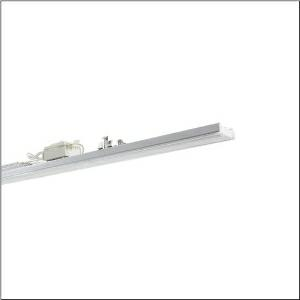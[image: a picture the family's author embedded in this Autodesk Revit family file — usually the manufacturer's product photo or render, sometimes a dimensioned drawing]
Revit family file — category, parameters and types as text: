
# Revit family: licross_r__21_recessed_mo_52tl14dv4exg_de02
name_source: partatom
category: Lighting Fixtures
units: mm (PartAtom-declared; Revit-internal decimal feet)

## family parameters
Cut with Voids When Loaded = No
Host = Face
Light Source = No
Part Type = Normal
Room Calculation Point = No
Round Connector Dimension = Use Diameter
Shared = No

## types (1)
- --- (1 x LED, 14200 lm, 85.3 W, 4000K)
    Apparent Load = 85 VA
    CIE Flux Codes = 56 84 97 100 100
    Color Rendering = 80
    Color Temperature = 4000K
    Default Elevation = 1800 mm
    Description = Licross® 21 Recessed MO, luminaire insert, of sheet steel, galvanised, coil coated, white, length: 2.250mm, width: 66mm, height: 67mm, LED rated luminous flux: 14.200lm, light colour: 840, control gear: DALI 2, with plug, 5-pole, with phase selection, mains connection: 220..240V, AC, 50/60Hz, rated input power: 85W, halogen-free wiring, primary light control with lens, of plastic, primary optical cover: cover, of PMMA, light emission: direct distribution, primary light characteristic: asymmetric, protection rating (complete): IP40, insulation class (complete): insulation class I (protective earthing), certification: CE, ENEC, VDE, UKCA, protection symbol: D if used in an environment without relevant dust loads with corresponding accessories, impact resistance: IK06, permissible ambient temperature for indoor applications: -25..+35°C, corresponds to IFS (International Featured Standards) requirements for safety and quality in the food industry, reducing of maximum allowable ambient temperature of 5°C with ceiling mounting, LABS conformity tested according to VDMA 24364:2018-05, packaging unit: 1 piece
    Height = 58 mm
    Lamp = 1 x LED
    Lamp Light Flux = 14200 lm
    Lamp Power = 85.3 W
    Lamp count = 1
    Length = 2250 mm
    Luminous efficacy = 166 lm/W
    Manufacturer = Siteco
    ModVariant = No
    Model = 52TL14DV4EXG
    Mounting Place = Ceiling
    Mounting Type = Pendant
    Number of Poles = 1
    OnlyDefault = Yes
    Power Factor = 1
    Product Name = Licross® 21 Recessed MO
    Product group = luminaire insert
    ProductGroupID = 902
    Protection Class = Protection class I
    Protection Degree = IP 40
    RLX_Detail_Level = 1
    RLX_Emergency_Light_Flux = 0 lm
    RLX_Emergency_Type = 0
    RLX_Emergency_Type_DB = No
    RlxData = <blob elided: 30037 chars, md5=b77f6273>
    Socket = socket
    Standby Power = 0 W
    System Light Flux = 14200 lm
    System Power = 85 W
    Type Comments = factory setting: luminous flux: 100 % | dim-lin: 254 | 390 mA
    Type Image = l_1296930.jpg
    URL = http://relux.com
    VarID = @adj_127842
    Voltage = 0 V
    Weight = 0.00 kg
    Width = 66 mm

## geometry (parser evidence)
native form markers: Blend x4, Sweep x11
no freeform markers — native parametric forms only
